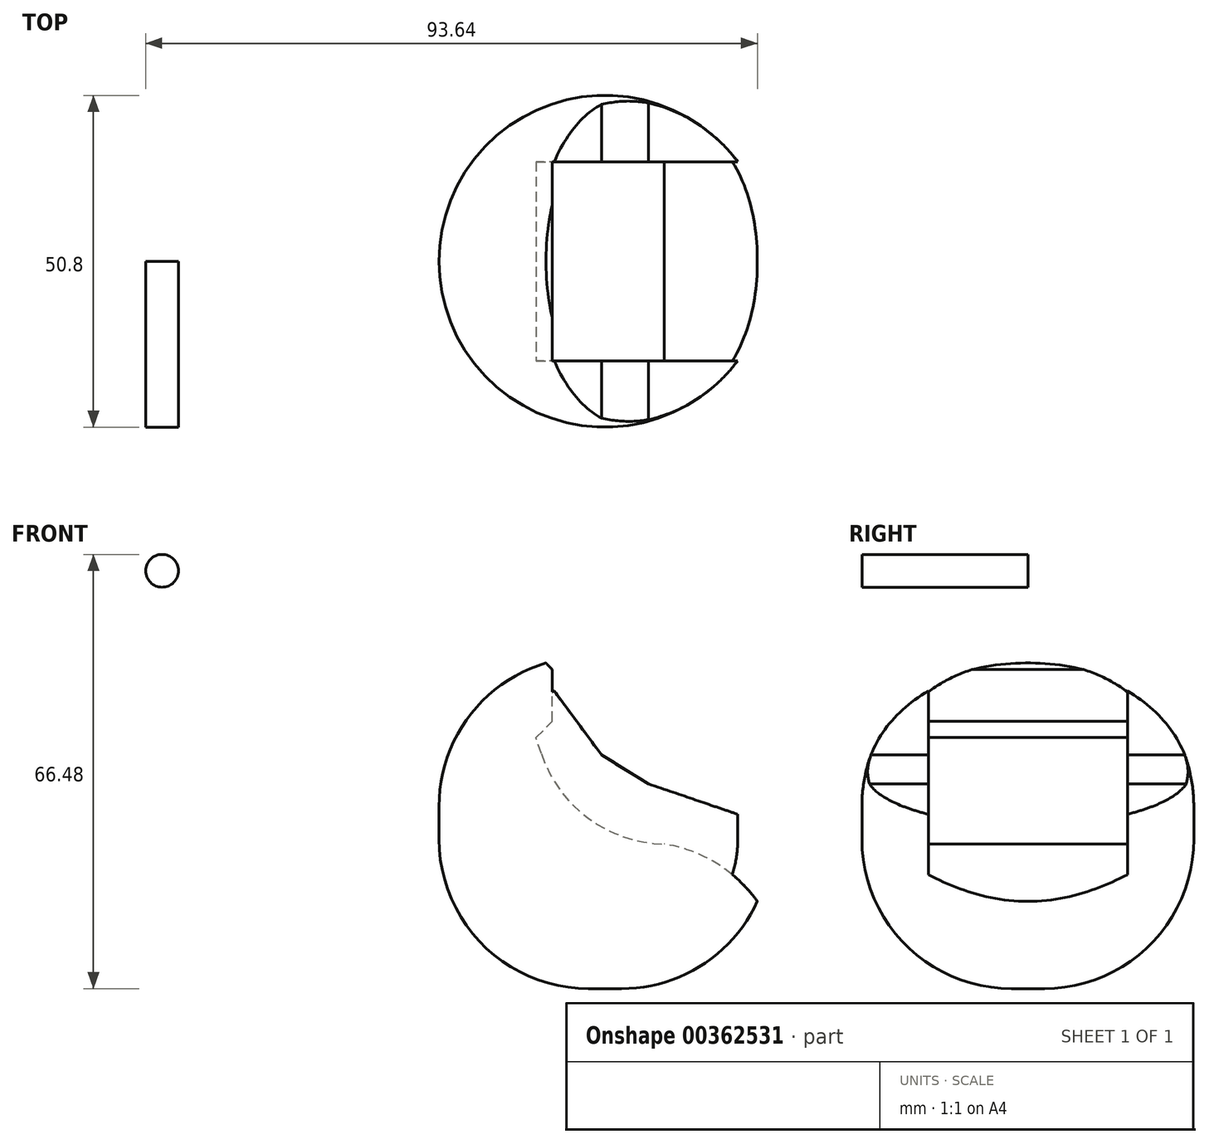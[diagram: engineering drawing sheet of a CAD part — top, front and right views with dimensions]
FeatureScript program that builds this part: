
annotation { "Feature Type Name" : "Feature", "Feature Type Description" : "" }
export const myFeature = defineFeature(function(context is Context, id is Id, definition is map)
    precondition{}
    {
        {
            var Q0;
            Q0=qCreatedBy(makeId("Top.planeOp"),FACE);
            var sketch = newSketch(context, id + "F0", { "sketchPlane" : qUnion([Q0])});
            skLineSegment(sketch, "E0.bottom", {"start": v(0, 0) * mm, "end": v(50.8, 0) * mm});
            skLineSegment(sketch, "E0.top", {"start": v(0, 50.8) * mm, "end": v(50.8, 50.8) * mm});
            skLineSegment(sketch, "E0.left", {"start": v(0, 0) * mm, "end": v(0, 50.8) * mm});
            skLineSegment(sketch, "E0.right", {"start": v(50.8, 0) * mm, "end": v(50.8, 50.8) * mm});
            skSolve(sketch);
        }
        {
            var Q0;
            Q0=makeQuery(id+"F0.imprint","IMPRINT",FACE,{"disambiguationData":[TD([[makeQuery(id+"F0.imprint","IMPRINT",EDGE,{"derivedFrom":sQuery(id+"F0.wireOp",EDGE,"E0.bottom")}),1.0]])]});
            extrude(context, id + "F1", {"entities" : qUnion([Q0]), "depth" : 50.8 * mm});
        }
        {
            var Q0;
            Q0=makeQuery(id+"F1.opExtrude","CAP_FACE",FACE,{"disambiguationData":[OSD([sQuery(id+"F0.wireOp",EDGE,"E0.bottom"),sQuery(id+"F0.wireOp",EDGE,"E0.top"),sQuery(id+"F0.wireOp",EDGE,"E0.left"),sQuery(id+"F0.wireOp",EDGE,"E0.right")])],"isStart":false});
            var sketch = newSketch(context, id + "F2", { "sketchPlane" : qUnion([Q0])});
            skLineSegment(sketch, "E1", {"start": v(0, 0) * mm, "end": v(0, 25.4) * mm});
            skLineSegment(sketch, "E2", {"start": v(0, 25.4) * mm, "end": v(25.4, 25.4) * mm});
            skCircle(sketch, "E3", {"center": v(25.4, 25.4) * mm, "radius": 25.4 * mm});
            skLineSegment(sketch, "E4.bottom", {"start": v(-31.7, 64.9) * mm, "end": v(143.61, 64.9) * mm});
            skLineSegment(sketch, "E4.top", {"start": v(-31.7, -36.69) * mm, "end": v(143.61, -36.69) * mm});
            skLineSegment(sketch, "E4.left", {"start": v(-31.7, 64.9) * mm, "end": v(-31.7, -36.69) * mm});
            skLineSegment(sketch, "E4.right", {"start": v(143.61, 64.9) * mm, "end": v(143.61, -36.69) * mm});
            skSolve(sketch);
        }
        {
            var Q0;
            Q0 = qSketchRegion(id + "F2", true);
            extrude(context, id + "F3", {"entities" : qUnion([Q0]), "operationType" : NewBodyOperationType.REMOVE, "oppositeDirection" : true, "depth" : 76.2 * mm});
        }
        {
            var Q0;
            Q0=makeQuery(id+"F1.opExtrude","CAP_FACE",FACE,{"disambiguationData":[OSD([sQuery(id+"F0.wireOp",EDGE,"E0.bottom"),sQuery(id+"F0.wireOp",EDGE,"E0.top"),sQuery(id+"F0.wireOp",EDGE,"E0.left"),sQuery(id+"F0.wireOp",EDGE,"E0.right")])],"isStart":false});
            var Q1;
            Q1=makeQuery(id+"F3.boolean.opBoolean","INTERSECT",EDGE,{"derivedFrom":[makeQuery(id+"F1.opExtrude","CAP_FACE",FACE,{"disambiguationData":[OSD([sQuery(id+"F0.wireOp",EDGE,"E0.bottom"),sQuery(id+"F0.wireOp",EDGE,"E0.top"),sQuery(id+"F0.wireOp",EDGE,"E0.left"),sQuery(id+"F0.wireOp",EDGE,"E0.right")])],"isStart":true}),makeQuery(id+"F3.opExtrude","SWEPT_FACE",FACE,{"disambiguationData":[OSD([sQuery(id+"F2.wireOp",EDGE,"E3")])]})]});
            fillet(context, id + "F4", {"entities" : qUnion([Q0, Q1]), "radius" : 22.86 * mm, "tangentPropagation" : true, "allowEdgeOverflow" : false});
        }
        {
            var Q0;
            Q0=qCreatedBy(makeId("Front.planeOp"),FACE);
            var sketch = newSketch(context, id + "F5", { "sketchPlane" : qUnion([Q0])});
            skCircle(sketch, "E5", {"center": v(-42.4, 63.97) * mm, "radius": 2.5 * mm});
            skSolve(sketch);
        }
        {
            var Q0;
            Q0=makeQuery(id+"F5.imprint","IMPRINT",FACE,{"disambiguationData":[TD([[makeQuery(id+"F5.imprint","IMPRINT",EDGE,{"derivedFrom":sQuery(id+"F5.wireOp",EDGE,"E5")}),1.0]])]});
            extrude(context, id + "F6", {"entities" : qUnion([Q0]), "oppositeDirection" : true, "depth" : 25.4 * mm});
        }
        {
            var Q0;
            Q0=makeQuery(id+"F6.opExtrude","CAP_FACE",FACE,{"disambiguationData":[OSD([sQuery(id+"F5.wireOp",EDGE,"E5")])],"isStart":false});
            var sketch = newSketch(context, id + "F7", { "sketchPlane" : qUnion([Q0])});
            skArc(sketch, "E6", {"start": v(-34.47, 22.12) * mm, "mid": v(-44.27, 17.94) * mm, "end": v(-50.88, 9.59) * mm});
            skArc(sketch, "E7", {"start": v(-34.47, 22.12) * mm, "mid": v(-22.88, 26.05) * mm, "end": v(-15.67, 35.95) * mm});
            skLineSegment(sketch, "E8", {"start": v(-15.67, 35.95) * mm, "end": v(-14.84, 38.44) * mm});
            skLineSegment(sketch, "E9", {"start": v(-14.84, 38.44) * mm, "end": v(-17.33, 40.93) * mm});
            skLineSegment(sketch, "E10", {"start": v(-17.33, 40.93) * mm, "end": v(-17.33, 48.85) * mm});
            skLineSegment(sketch, "E11", {"start": v(-17.33, 48.85) * mm, "end": v(-14.84, 51.44) * mm});
            skLineSegment(sketch, "E12", {"start": v(-14.84, 51.44) * mm, "end": v(-53.1, 56.78) * mm});
            skLineSegment(sketch, "E13", {"start": v(-53.1, 56.78) * mm, "end": v(-59.18, 29.31) * mm});
            skLineSegment(sketch, "E14", {"start": v(-59.18, 29.31) * mm, "end": v(-60.84, 14.38) * mm});
            skLineSegment(sketch, "E15", {"start": v(-60.84, 14.38) * mm, "end": v(-50.88, 9.59) * mm});
            skSolve(sketch);
        }
        {
            var Q0;
            Q0 = qSketchRegion(id + "F7", true);
            extrude(context, id + "F8", {"entities" : qUnion([Q0]), "operationType" : NewBodyOperationType.REMOVE, "depth" : 30.48 * mm, "symmetric" : true});
        }
        {
            var Q0;
            Q0=makeQuery(id+"F6.opExtrude","CAP_FACE",FACE,{"disambiguationData":[OSD([sQuery(id+"F5.wireOp",EDGE,"E5")])],"isStart":false});
            var sketch = newSketch(context, id + "F9", { "sketchPlane" : qUnion([Q0])});
            skLineSegment(sketch, "E16", {"start": v(-17.51, 45.72) * mm, "end": v(-24.89, 35.76) * mm});
            skLineSegment(sketch, "E17", {"start": v(-24.89, 35.76) * mm, "end": v(-32.08, 31.34) * mm});
            skLineSegment(sketch, "E18", {"start": v(-32.08, 31.34) * mm, "end": v(-48.3, 25.8) * mm});
            skLineSegment(sketch, "E19", {"start": v(-48.3, 25.8) * mm, "end": v(-64.34, 40.37) * mm});
            skLineSegment(sketch, "E20", {"start": v(-64.34, 40.37) * mm, "end": v(-41.48, 56.6) * mm});
            skLineSegment(sketch, "E21", {"start": v(-41.48, 56.6) * mm, "end": v(-17.51, 45.72) * mm});
            skSolve(sketch);
        }
        {
            var Q0;
            Q0 = qSketchRegion(id + "F9", true);
            extrude(context, id + "F10", {"entities" : qUnion([Q0]), "operationType" : NewBodyOperationType.REMOVE, "depth" : 78.74 * mm, "symmetric" : true});
        }
    });
